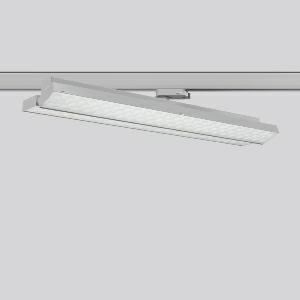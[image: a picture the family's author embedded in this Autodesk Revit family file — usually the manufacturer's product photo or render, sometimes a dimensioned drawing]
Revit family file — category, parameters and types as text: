
# Revit family: tx-move_742162_004_1_0ecb
name_source: partatom
category: Lighting Fixtures
units: mm (PartAtom-declared; Revit-internal decimal feet)

## family parameters
Cut with Voids When Loaded = No
Host = Face
Light Source = No
Part Type = Normal
Room Calculation Point = No
Round Connector Dimension = Use Diameter
Shared = No

## types (1)
- MultiLumen 1 (1 x LED Modul 840, 3150 lm, 4000)
    Apparent Load = 41 VA
    CIE Flux Codes = 77 96 99 100 100
    Color Rendering = 80
    Color Temperature = 4000
    Default Elevation = 1800 mm
    Description = Series: TX-MOVE
Multifunctional surface-mounted spotlight for area lighting. Very flat design. Housing: sheet steel, powder-coated. Rotation range: 356°. Swivel range: 90°. Consistent alignment possible with visible tilt scale. High-efficiency LED units with optimum light control thanks to clear plastic (PC) lens optics. Spezielle Mikrostrukturen reduzieren Gelbsaum. Symmetrical light distribution. With multi adaptor for 3-circuit tracks 230 V. Suitable for Track on ceiling. MultiLumen: Luminous flux adjustable in 3 steps. Factory setting is the highest luminous flux. Environmentally friendly and resource-saving due to replaceable and recyclable components. 
Colour: silver, matt (approx. RAL 9006)
Length: 570 mm
Width: 119 mm
Height: 92 mm
Lamp: LED
Socket: without socket
Colour temperature: 4000K
Colour rendering index (CRI): 80
System power: 41 W
Rated luminous flux: 6300 lm
Luminous efficiency: 154 lm/W
System power 2: 57 W
Rated luminous flux 2: 8550 lm
Luminous efficiency 2: 150 lm/W
System power 3: 73 W
Rated luminous flux 3: 10400 lm
Luminous efficiency 3: 142 lm/W
Control gear: Regulated power supply
Protection class: I
Type of protection: IP 20
    Height = 75 mm
    Lamp = 1 x LED Modul 840
    Lamp Light Flux = 3150 lm
    Lamp count = 1
    Length = 569 mm
    Lifetime = 50000 h
    Luminous efficacy = 154 lm/W
    Manufacturer = RZB
    ModVariant = No
    Model = 742162.004.1
    Mounting Place = Ceiling
    Mounting Type = Surface mounted
    Number of Poles = 1
    OnlyDefault = Yes
    Power Factor = 1
    Product Name = TX-MOVE
    Product group = Track mounted projectors
    ProductGroupID = 301
    Protection Class = Protection class I
    Protection Degree = IP 20
    RLX_Detail_Level = 1
    RLX_Emergency_Light_Flux = 0 lm
    RLX_Emergency_Type = 0
    RLX_Emergency_Type_DB = No
    RlxData = <blob elided: 33229 chars, md5=0ac8c2f0>
    Socket = socket
    Standby Power = 0 W
    System Light Flux = 6300 lm
    System Power = 41 W
    Type Comments = MultiLumen 1
    Type Image = 742162.004.jpg
    URL = http://relux.com
    VarID = multilumen_1
    Voltage = 0 V
    Weight = 0.00 kg
    Width = 119 mm

## geometry (parser evidence)
native form markers: Blend x4, Sweep x16
no freeform markers — native parametric forms only
